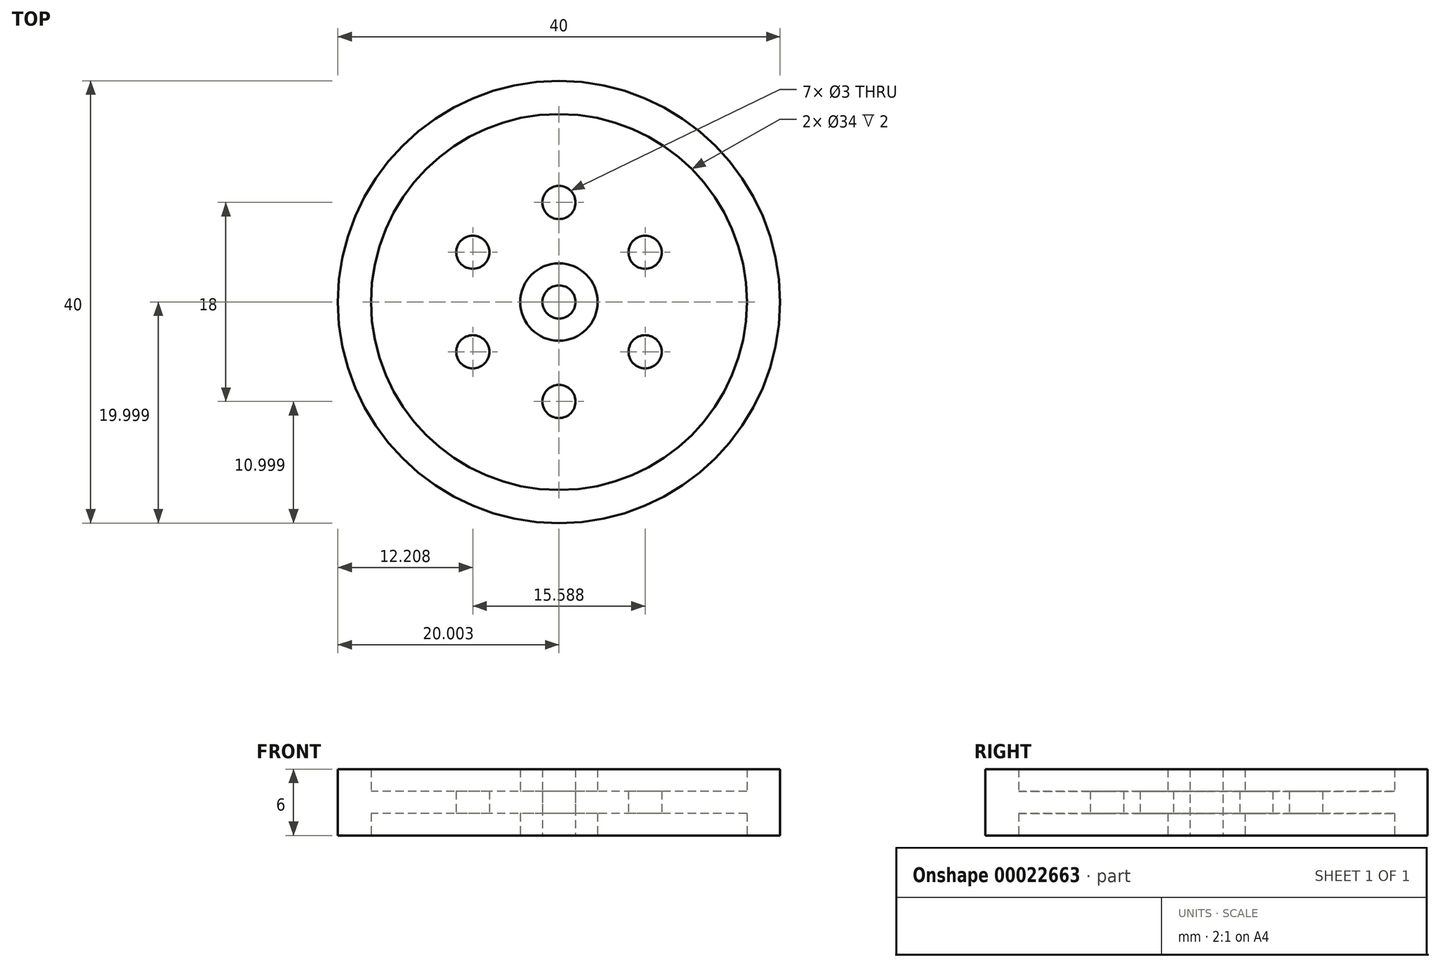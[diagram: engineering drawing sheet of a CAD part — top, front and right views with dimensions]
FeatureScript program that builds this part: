
annotation { "Feature Type Name" : "Feature", "Feature Type Description" : "" }
export const myFeature = defineFeature(function(context is Context, id is Id, definition is map)
    precondition{}
    {
        {
            var Q0;
            Q0=qCreatedBy(makeId("Top.planeOp"),FACE);
            var sketch = newSketch(context, id + "F0", { "sketchPlane" : qUnion([Q0])});
            skCircle(sketch, "E0", {"center": v(-13.7, -1.34) * mm, "radius": 20 * mm});
            skCircle(sketch, "E1", {"center": v(-13.7, -1.34) * mm, "radius": 17 * mm});
            skCircle(sketch, "E2", {"center": v(-13.7, -1.34) * mm, "radius": 3.5 * mm});
            skCircle(sketch, "E3", {"center": v(-13.7, 7.66) * mm, "radius": 1.5 * mm});
            skCircle(sketch, "E4", {"center": v(-13.7, -1.34) * mm, "radius": 1.5 * mm});
            skCircle(sketch, "E5.1.0", {"center": v(-21.5, 3.16) * mm, "radius": 1.5 * mm});
            skCircle(sketch, "E5.2.0", {"center": v(-21.5, -5.84) * mm, "radius": 1.5 * mm});
            skCircle(sketch, "E5.3.0", {"center": v(-13.7, -10.34) * mm, "radius": 1.5 * mm});
            skCircle(sketch, "E5.4.0", {"center": v(-5.91, -5.84) * mm, "radius": 1.5 * mm});
            skCircle(sketch, "E5.5.0", {"center": v(-5.91, 3.16) * mm, "radius": 1.5 * mm});
            skSolve(sketch);
        }
        {
            var Q0;
            Q0=makeQuery(id+"F0.imprint","IMPRINT",FACE,{"disambiguationData":[TD([[makeQuery(id+"F0.imprint","IMPRINT",EDGE,{"derivedFrom":sQuery(id+"F0.wireOp",EDGE,"E0")}),1.0]])]});
            var Q1;
            Q1=makeQuery(id+"F0.imprint","IMPRINT",FACE,{"disambiguationData":[TD([[makeQuery(id+"F0.imprint","IMPRINT",EDGE,{"derivedFrom":sQuery(id+"F0.wireOp",EDGE,"E2")}),1.0]])]});
            extrude(context, id + "F1", {"entities" : qUnion([Q0, Q1]), "depth" : 6 * mm});
        }
        {
            var Q0;
            Q0=makeQuery(id+"F0.imprint","IMPRINT",FACE,{"disambiguationData":[TD([[makeQuery(id+"F0.imprint","IMPRINT",EDGE,{"derivedFrom":sQuery(id+"F0.wireOp",EDGE,"E1")}),1.0]])]});
            extrude(context, id + "F2", {"entities" : qUnion([Q0]), "operationType" : NewBodyOperationType.ADD, "depth" : 4 * mm});
        }
        {
            var Q0;
            Q0=makeQuery(id+"F0.imprint","IMPRINT",FACE,{"disambiguationData":[TD([[makeQuery(id+"F0.imprint","IMPRINT",EDGE,{"derivedFrom":sQuery(id+"F0.wireOp",EDGE,"E1")}),1.0]])]});
            extrude(context, id + "F3", {"entities" : qUnion([Q0]), "operationType" : NewBodyOperationType.REMOVE, "depth" : 2 * mm});
        }
    });
